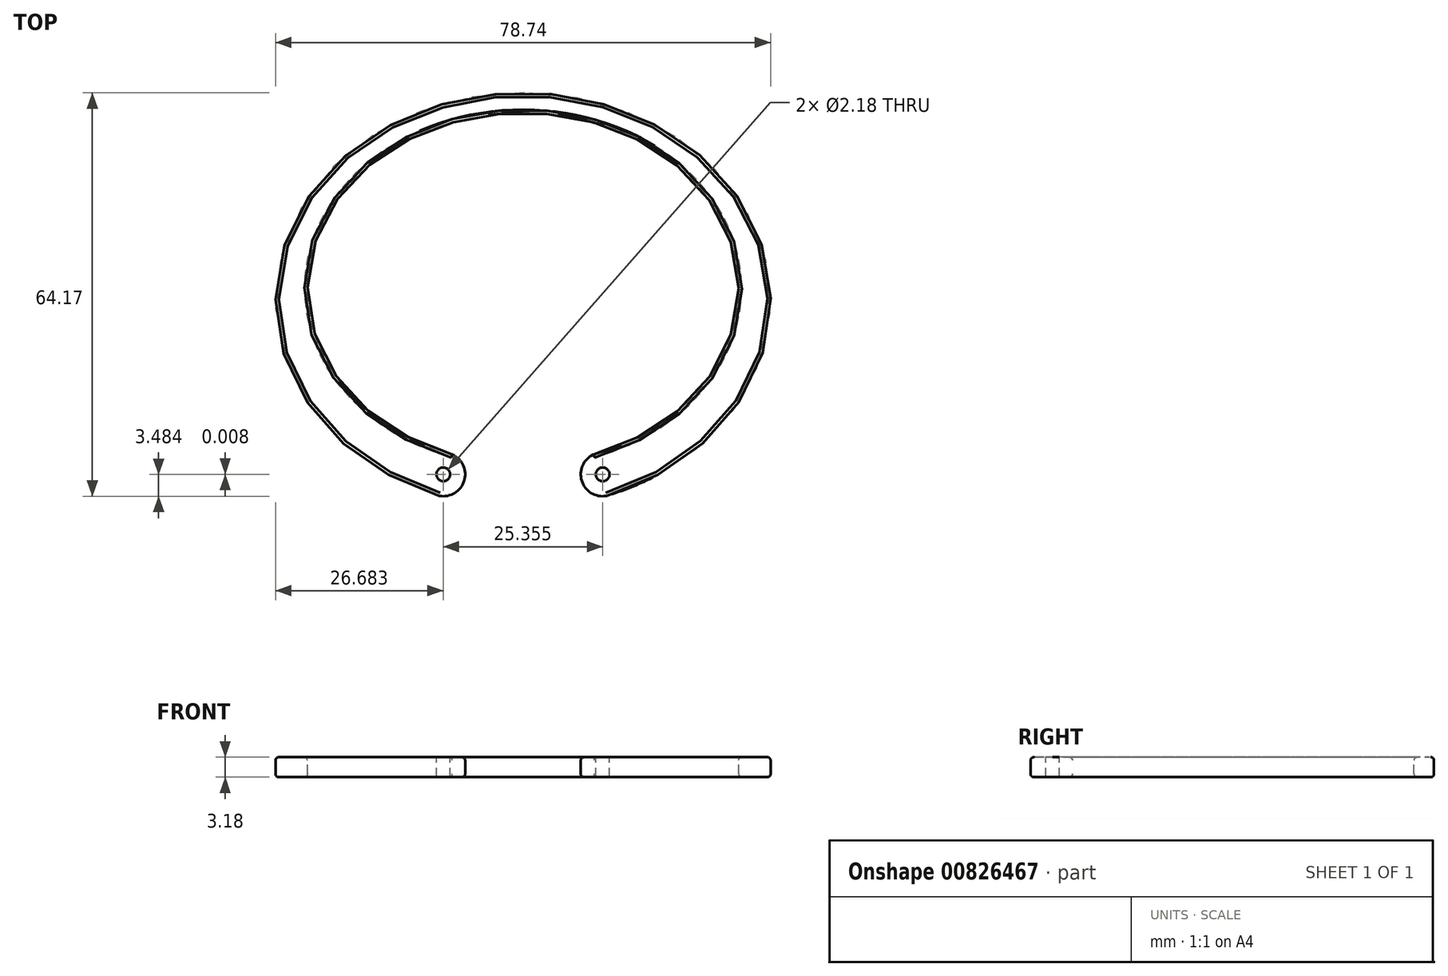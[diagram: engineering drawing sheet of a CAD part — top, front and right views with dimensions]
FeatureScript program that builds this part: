
annotation { "Feature Type Name" : "Feature", "Feature Type Description" : "" }
export const myFeature = defineFeature(function(context is Context, id is Id, definition is map)
    precondition{}
    {
        {
            var Q0;
            Q0=qCreatedBy(makeId("Top.planeOp"),FACE);
            var sketch = newSketch(context, id + "F0", { "sketchPlane" : qUnion([Q0])});
            skEllipse(sketch, "E0", {"center": v(0, 0) * mm, "majorRadius": 34.3 * mm, "minorRadius": 27.94 * mm, "majorAxis": v(1, 0)});
            skEllipse(sketch, "E1", {"center": v(0, -1.9) * mm, "majorRadius": 39.37 * mm, "minorRadius": 33.02 * mm, "majorAxis": v(1, 0)});
            skLineSegment(sketch, "E2", {"start": v(0, 0) * mm, "end": v(0, 27.94) * mm});
            skPoint(sketch, "E3", {"position": v(0, 31.12) * mm});
            skLineSegment(sketch, "E4", {"start": v(-12.7, 0) * mm, "end": v(12.7, 0) * mm});
            skLineSegment(sketch, "E5", {"start": v(-12.7, 7.48) * mm, "end": v(12.7, 7.48) * mm});
            skLineSegment(sketch, "E6", {"start": v(0, -27.94) * mm, "end": v(0, -34.93) * mm});
            skPoint(sketch, "E7", {"position": v(0, -31.43) * mm});
            skPoint(sketch, "E8", {"position": v(-36.8, 0) * mm});
            skPoint(sketch, "E9", {"position": v(36.8, 0) * mm});
            skPoint(sketch, "E10", {"position": v(0, 29.53) * mm});
            skEllipticalArc(sketch, "E11", {});
            skEllipticalArc(sketch, "E12", {});
            skLineSegment(sketch, "E13", {"start": v(0, -1.9) * mm, "end": v(-12.7, -29.63) * mm});
            skLineSegment(sketch, "E14", {"start": v(0, -1.9) * mm, "end": v(12.7, -29.63) * mm});
            skLineSegment(sketch, "E15", {"start": v(-12.7, -29.63) * mm, "end": v(-14.12, -32.73) * mm});
            skLineSegment(sketch, "E16", {"start": v(12.7, -29.63) * mm, "end": v(14.12, -32.73) * mm});
            skPoint(sketch, "E17", {"position": v(-11.22, -26.4) * mm});
            skPoint(sketch, "E18", {"position": v(11.22, -26.4) * mm});
            skArc(sketch, "E19", {"start": v(-14.12, -32.73) * mm, "mid": v(-9.52, -31) * mm, "end": v(-11.22, -26.4) * mm});
            skArc(sketch, "E20", {"start": v(11.22, -26.4) * mm, "mid": v(9.5, -31.01) * mm, "end": v(14.12, -32.73) * mm});
            skLineSegment(sketch, "E21", {"start": v(-12.7, 7.48) * mm, "end": v(-21.17, 7.48) * mm});
            skLineSegment(sketch, "E22", {"start": v(12.7, 7.48) * mm, "end": v(21.17, 7.48) * mm});
            skLineSegment(sketch, "E23", {"start": v(0, 0) * mm, "end": v(-21.17, -26.11) * mm});
            skLineSegment(sketch, "E24", {"start": v(-21.17, -26.11) * mm, "end": v(-23.18, -28.6) * mm});
            skLineSegment(sketch, "E25", {"start": v(0, 0) * mm, "end": v(21.17, -26.11) * mm});
            skLineSegment(sketch, "E26", {"start": v(21.17, -26.11) * mm, "end": v(23.18, -28.6) * mm});
            skArc(sketch, "E27", {"start": v(-11.22, -26.4) * mm, "mid": v(-15.86, -28.1) * mm, "end": v(-14.12, -32.73) * mm});
            skArc(sketch, "E28", {"start": v(14.12, -32.73) * mm, "mid": v(15.8, -28.13) * mm, "end": v(11.22, -26.4) * mm});
            const initialGuessF0  = {"E11": [0, 0, 1, 0, 0.036797212894794956, 0.029527500000000005, 0, 3.141592653589793], "E12": [0, -0.001905, 1, 0, 0.03696378320455551, 0.02952750000000001, 3.039564363503366, 0.10202829008642726]};
            skSetInitialGuess(sketch, initialGuessF0);
            skSolve(sketch);
        }
        {
            var Q0;
            {var subQ0=sQuery(id+"F0.wireOp",EDGE,"E27");var subQ2=sQuery(id+"F0.wireOp",EDGE,"E0");var subQ4=makeQuery(id+"F0.imprint","INTERSECT",VERTEX,{"derivedFrom":[subQ2,subQ0]});Q0=makeQuery(id+"F0.imprint","IMPRINT",FACE,{"disambiguationData":[TD([[makeQuery(id+"F0.imprint","IMPRINT",EDGE,{"disambiguationData":[TD([[subQ4,-1.0]])],"derivedFrom":subQ0}),1.0]])]});}
            var Q1;
            {var subQ1=sQuery(id+"F0.wireOp",EDGE,"E12");var subQ3=sQuery(id+"F0.wireOp",EDGE,"E19");var subQ4=makeQuery(id+"F0.imprint","INTERSECT",VERTEX,{"derivedFrom":[subQ1,subQ3]});Q1=makeQuery(id+"F0.imprint","IMPRINT",FACE,{"disambiguationData":[TD([[makeQuery(id+"F0.imprint","IMPRINT",EDGE,{"disambiguationData":[TD([[subQ4,1.0]])],"derivedFrom":subQ1}),1.0]])]});}
            var Q2;
            {var subQ1=sQuery(id+"F0.wireOp",EDGE,"E15");Q2=makeQuery(id+"F0.imprint","IMPRINT",FACE,{"disambiguationData":[TD([[makeQuery(id+"F0.imprint","IMPRINT",EDGE,{"derivedFrom":subQ1}),1.0]])]});}
            var Q3;
            {var subQ0=sQuery(id+"F0.wireOp",EDGE,"E15");Q3=makeQuery(id+"F0.imprint","IMPRINT",FACE,{"disambiguationData":[TD([[makeQuery(id+"F0.imprint","IMPRINT",EDGE,{"derivedFrom":subQ0}),-1.0]])]});}
            var Q4;
            {var subQ0=sQuery(id+"F0.wireOp",EDGE,"E23");var subQ1=sQuery(id+"F0.wireOp",EDGE,"E0");var subQ2=makeQuery(id+"F0.imprint","INTERSECT",VERTEX,{"derivedFrom":[subQ1,subQ0]});Q4=makeQuery(id+"F0.imprint","IMPRINT",FACE,{"disambiguationData":[TD([[makeQuery(id+"F0.imprint","IMPRINT",EDGE,{"disambiguationData":[TD([[subQ2,-1.0]])],"derivedFrom":subQ1}),-1.0]])]});}
            var Q5;
            {var subQ3=sQuery(id+"F0.wireOp",EDGE,"E24");Q5=makeQuery(id+"F0.imprint","IMPRINT",FACE,{"disambiguationData":[TD([[makeQuery(id+"F0.imprint","IMPRINT",EDGE,{"derivedFrom":subQ3}),1.0]])]});}
            var Q6;
            {var subQ4=sQuery(id+"F0.wireOp",EDGE,"E0");var subQ5=makeQuery(id+"F0.imprint","INTERSECT",VERTEX,{"derivedFrom":[subQ4,sQuery(id+"F0.wireOp",EDGE,"E2")]});Q6=makeQuery(id+"F0.imprint","IMPRINT",FACE,{"disambiguationData":[TD([[makeQuery(id+"F0.imprint","IMPRINT",EDGE,{"disambiguationData":[TD([[subQ5,-1.0]])],"derivedFrom":subQ4}),-1.0]])]});}
            var Q7;
            {var subQ3=sQuery(id+"F0.wireOp",EDGE,"E24");Q7=makeQuery(id+"F0.imprint","IMPRINT",FACE,{"disambiguationData":[TD([[makeQuery(id+"F0.imprint","IMPRINT",EDGE,{"derivedFrom":subQ3}),-1.0]])]});}
            var Q8;
            {var subQ0=sQuery(id+"F0.wireOp",EDGE,"E28");var subQ2=sQuery(id+"F0.wireOp",EDGE,"E0");var subQ4=makeQuery(id+"F0.imprint","INTERSECT",VERTEX,{"derivedFrom":[subQ2,subQ0]});Q8=makeQuery(id+"F0.imprint","IMPRINT",FACE,{"disambiguationData":[TD([[makeQuery(id+"F0.imprint","IMPRINT",EDGE,{"disambiguationData":[TD([[subQ4,1.0]])],"derivedFrom":subQ0}),1.0]])]});}
            var Q9;
            {var subQ1=sQuery(id+"F0.wireOp",EDGE,"E12");var subQ3=sQuery(id+"F0.wireOp",EDGE,"E20");var subQ4=makeQuery(id+"F0.imprint","INTERSECT",VERTEX,{"derivedFrom":[subQ1,subQ3]});Q9=makeQuery(id+"F0.imprint","IMPRINT",FACE,{"disambiguationData":[TD([[makeQuery(id+"F0.imprint","IMPRINT",EDGE,{"disambiguationData":[TD([[subQ4,-1.0]])],"derivedFrom":subQ1}),1.0]])]});}
            var Q10;
            {var subQ1=sQuery(id+"F0.wireOp",EDGE,"E16");Q10=makeQuery(id+"F0.imprint","IMPRINT",FACE,{"disambiguationData":[TD([[makeQuery(id+"F0.imprint","IMPRINT",EDGE,{"derivedFrom":subQ1}),-1.0]])]});}
            var Q11;
            {var subQ0=sQuery(id+"F0.wireOp",EDGE,"E16");Q11=makeQuery(id+"F0.imprint","IMPRINT",FACE,{"disambiguationData":[TD([[makeQuery(id+"F0.imprint","IMPRINT",EDGE,{"derivedFrom":subQ0}),1.0]])]});}
            var Q12;
            {var subQ3=sQuery(id+"F0.wireOp",EDGE,"E26");Q12=makeQuery(id+"F0.imprint","IMPRINT",FACE,{"disambiguationData":[TD([[makeQuery(id+"F0.imprint","IMPRINT",EDGE,{"derivedFrom":subQ3}),-1.0]])]});}
            var Q13;
            {var subQ0=sQuery(id+"F0.wireOp",EDGE,"E28");var subQ1=sQuery(id+"F0.wireOp",EDGE,"E0");var subQ2=makeQuery(id+"F0.imprint","INTERSECT",VERTEX,{"derivedFrom":[subQ1,subQ0]});Q13=makeQuery(id+"F0.imprint","IMPRINT",FACE,{"disambiguationData":[TD([[makeQuery(id+"F0.imprint","IMPRINT",EDGE,{"disambiguationData":[TD([[subQ2,-1.0]])],"derivedFrom":subQ1}),-1.0]])]});}
            extrude(context, id + "F1", {"entities" : qUnion([Q0, Q1, Q2, Q3, Q4, Q5, Q6, Q7, Q8, Q9, Q10, Q11, Q12, Q13]), "depth" : 3.17 * mm, "offsetDistance" : 25.4 * mm});
        }
        {
            var Q0;
            Q0=makeQuery(id+"F1.opExtrude","CAP_FACE",FACE,{"disambiguationData":[OSD([sQuery(id+"F0.wireOp",EDGE,"E0"),sQuery(id+"F0.wireOp",EDGE,"E1"),sQuery(id+"F0.wireOp",EDGE,"E19"),sQuery(id+"F0.wireOp",EDGE,"E20")])],"isStart":false});
            var sketch = newSketch(context, id + "F2", { "sketchPlane" : qUnion([Q0])});
            skPoint(sketch, "E29", {"position": v(-12.69, -29.56) * mm});
            skPoint(sketch, "E30", {"position": v(12.67, -29.57) * mm});
            skSolve(sketch);
        }
        {
            var Q0;
            Q0=sQuery(id+"F2.wireOp",VERTEX,"E29");
            var Q1;
            Q1=sQuery(id+"F2.wireOp",VERTEX,"E30");
            var Q2;
            Q2=makeQuery(id+"F1.opExtrude","SWEPT_BODY",BODY,{"disambiguationData":[OSD([sQuery(id+"F0.wireOp",EDGE,"E0"),sQuery(id+"F0.wireOp",EDGE,"E1"),sQuery(id+"F0.wireOp",EDGE,"E19"),sQuery(id+"F0.wireOp",EDGE,"E20")])]});
            hole(context, id + "F3", {"style" : HoleStyle.SIMPLE, "endStyle" : HoleEndStyle.THROUGH, "holeDiameter" : 2.18 * mm, "majorDiameter" : 6.35 * mm, "isTappedThrough" : true, "tappedDepth" : 12.7 * mm, "tapClearance" : 3, "locations" : qUnion([Q0, Q1]), "scope" : qUnion([Q2])});
        }
        {
            var Q0;
            Q0=makeQuery(id+"F1.opExtrude","SWEPT_FACE",FACE,{"disambiguationData":[OSD([sQuery(id+"F0.wireOp",EDGE,"E0")])]});
            var Q1;
            Q1=makeQuery(id+"F1.opExtrude","SWEPT_FACE",FACE,{"disambiguationData":[OSD([sQuery(id+"F0.wireOp",EDGE,"E1")])]});
            var Q2;
            Q2=makeQuery(id+"F1.opExtrude","SWEPT_FACE",FACE,{"disambiguationData":[OSD([sQuery(id+"F0.wireOp",EDGE,"E19")])]});
            var Q3;
            Q3=makeQuery(id+"F1.opExtrude","SWEPT_FACE",FACE,{"disambiguationData":[OSD([sQuery(id+"F0.wireOp",EDGE,"E20")])]});
            fillet(context, id + "F4", {"entities" : qUnion([Q0, Q1, Q2, Q3]), "radius" : 0.5 * mm, "tangentPropagation" : true, "allowEdgeOverflow" : false});
        }
    });
